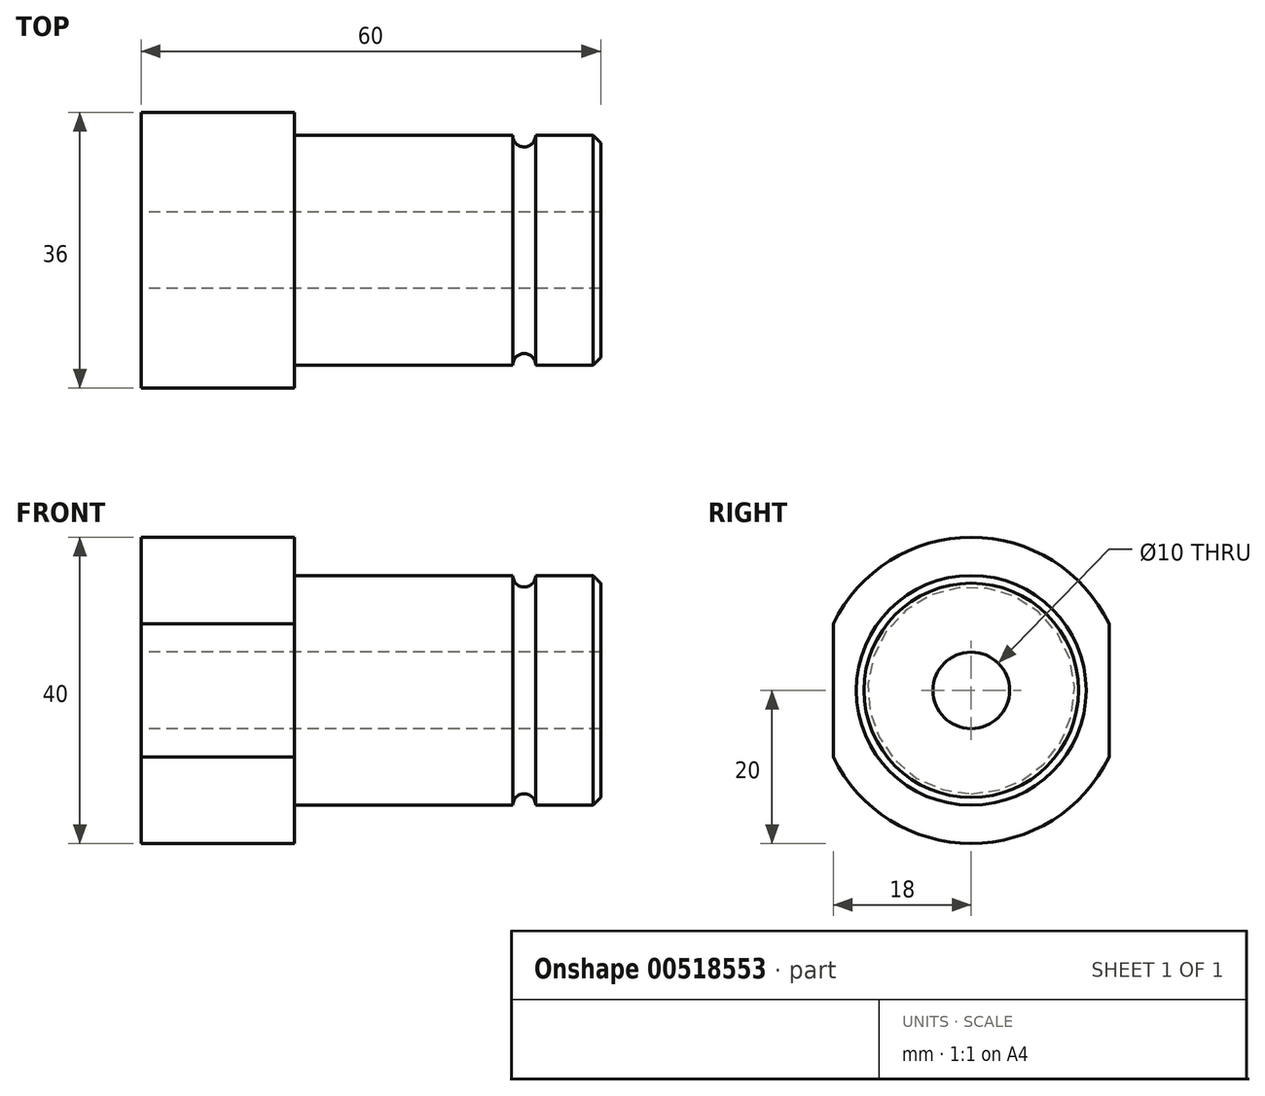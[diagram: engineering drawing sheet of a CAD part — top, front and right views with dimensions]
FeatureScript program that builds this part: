
annotation { "Feature Type Name" : "Feature", "Feature Type Description" : "" }
export const myFeature = defineFeature(function(context is Context, id is Id, definition is map)
    precondition{}
    {
        {
            var Q0;
            Q0=qCreatedBy(makeId("Top.planeOp"),FACE);
            var sketch = newSketch(context, id + "F0", { "sketchPlane" : qUnion([Q0])});
            skLineSegment(sketch, "E0", {"start": v(0, 0) * mm, "end": v(0, 20) * mm});
            skLineSegment(sketch, "E1", {"start": v(0, 20) * mm, "end": v(20, 20) * mm});
            skLineSegment(sketch, "E2", {"start": v(20, 20) * mm, "end": v(20, 15) * mm});
            skLineSegment(sketch, "E3", {"start": v(60, 15) * mm, "end": v(60, 0) * mm});
            skLineSegment(sketch, "E4", {"start": v(60, 0) * mm, "end": v(0, 0) * mm});
            skLineSegment(sketch, "E5", {"start": v(20, 15) * mm, "end": v(60, 15) * mm});
            skSolve(sketch);
        }
        {
            var Q0;
            Q0=makeQuery(id+"F0.imprint","IMPRINT",FACE,{"disambiguationData":[TD([[makeQuery(id+"F0.imprint","IMPRINT",EDGE,{"derivedFrom":sQuery(id+"F0.wireOp",EDGE,"E0")}),-1.0]])]});
            var Q1;
            Q1=sQuery(id+"F0.wireOp",EDGE,"E4");
            revolve(context, id + "F1", {"entities" : qUnion([Q0]), "axis" : qUnion([Q1]), "revolveType" : RevolveType.FULL});
        }
        {
            var Q0;
            Q0=makeQuery(id+"F1.opRevolve","SWEPT_EDGE",EDGE,{"disambiguationData":[OSD([sQuery(id+"F0.wireOp",EDGE,"E3"),sQuery(id+"F0.wireOp",EDGE,"E5")])]});
            chamfer(context, id + "F2", {"entities" : qUnion([Q0]), "width" : 1 * mm, "tangentPropagation" : true});
        }
        {
            var Q0;
            Q0=makeQuery(id+"F1.opRevolve","SWEPT_FACE",FACE,{"disambiguationData":[OSD([sQuery(id+"F0.wireOp",EDGE,"E0")])]});
            var sketch = newSketch(context, id + "F3", { "sketchPlane" : qUnion([Q0])});
            skLineSegment(sketch, "E6.bottom", {"start": v(-18, 62.27) * mm, "end": v(18, 62.27) * mm});
            skLineSegment(sketch, "E6.top", {"start": v(-18, -59.03) * mm, "end": v(18, -59.03) * mm});
            skLineSegment(sketch, "E6.left", {"start": v(-18, 62.27) * mm, "end": v(-18, -59.03) * mm});
            skLineSegment(sketch, "E6.right", {"start": v(18, 62.27) * mm, "end": v(18, -59.03) * mm});
            skSolve(sketch);
        }
        {
            var Q0;
            {var subQ0=sQuery(id+"F3.wireOp",EDGE,"E6.left");var subQ1=makeQuery(id+"F1.opRevolve","SWEPT_EDGE",EDGE,{"disambiguationData":[OSD([sQuery(id+"F0.wireOp",EDGE,"E0"),sQuery(id+"F0.wireOp",EDGE,"E1")])]});var subQ2=makeQuery(id+"F3.imprint","INTERSECT",VERTEX,{"disambiguationData":[OD(0.0)],"derivedFrom":[subQ1,subQ0]});Q0=makeQuery(id+"F3.imprint","IMPRINT",FACE,{"disambiguationData":[TD([[makeQuery(id+"F3.imprint","IMPRINT",EDGE,{"disambiguationData":[TD([[subQ2,-1.0]])],"derivedFrom":subQ0}),-1.0]])]});}
            var Q1;
            {var subQ0=sQuery(id+"F3.wireOp",EDGE,"E6.right");var subQ1=makeQuery(id+"F1.opRevolve","SWEPT_EDGE",EDGE,{"disambiguationData":[OSD([sQuery(id+"F0.wireOp",EDGE,"E0"),sQuery(id+"F0.wireOp",EDGE,"E1")])]});var subQ2=makeQuery(id+"F3.imprint","INTERSECT",VERTEX,{"disambiguationData":[OD(0.0)],"derivedFrom":[subQ1,subQ0]});Q1=makeQuery(id+"F3.imprint","IMPRINT",FACE,{"disambiguationData":[TD([[makeQuery(id+"F3.imprint","IMPRINT",EDGE,{"disambiguationData":[TD([[subQ2,-1.0]])],"derivedFrom":subQ0}),1.0]])]});}
            extrude(context, id + "F4", {"entities" : qUnion([Q0, Q1]), "operationType" : NewBodyOperationType.REMOVE, "endBound" : BoundingType.THROUGH_ALL, "oppositeDirection" : true, "depth" : 25 * mm, "offsetDistance" : 25 * mm});
        }
        {
            var Q0;
            Q0=makeQuery(id+"F1.opRevolve","SWEPT_FACE",FACE,{"disambiguationData":[OSD([sQuery(id+"F0.wireOp",EDGE,"E0")])]});
            var sketch = newSketch(context, id + "F5", { "sketchPlane" : qUnion([Q0])});
            skCircle(sketch, "E7", {"center": v(0, 0) * mm, "radius": 5 * mm});
            skSolve(sketch);
        }
        {
            var Q0;
            Q0=makeQuery(id+"F5.imprint","IMPRINT",FACE,{"disambiguationData":[TD([[makeQuery(id+"F5.imprint","IMPRINT",EDGE,{"derivedFrom":sQuery(id+"F5.wireOp",EDGE,"E7")}),1.0]])]});
            extrude(context, id + "F6", {"entities" : qUnion([Q0]), "operationType" : NewBodyOperationType.REMOVE, "endBound" : BoundingType.THROUGH_ALL, "oppositeDirection" : true, "depth" : 25 * mm, "offsetDistance" : 25 * mm});
        }
        {
            var Q0;
            Q0=qCreatedBy(makeId("Front.planeOp"),FACE);
            var sketch = newSketch(context, id + "F7", { "sketchPlane" : qUnion([Q0])});
            skCircle(sketch, "E8", {"center": v(50, 15) * mm, "radius": 1.5 * mm});
            skSolve(sketch);
        }
        {
            var Q0;
            Q0=makeQuery(id+"F7.imprint","IMPRINT",FACE,{"disambiguationData":[TD([[makeQuery(id+"F7.imprint","IMPRINT",EDGE,{"derivedFrom":sQuery(id+"F7.wireOp",EDGE,"E8")}),1.0]])]});
            var Q1;
            Q1=makeQuery(id+"F1.opRevolve","SWEPT_FACE",FACE,{"disambiguationData":[OSD([sQuery(id+"F0.wireOp",EDGE,"E5")])]});
            revolve(context, id + "F8", {"operationType" : NewBodyOperationType.REMOVE, "entities" : qUnion([Q0]), "axis" : qUnion([Q1]), "revolveType" : RevolveType.FULL, "oppositeDirection" : true});
        }
    });
